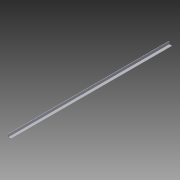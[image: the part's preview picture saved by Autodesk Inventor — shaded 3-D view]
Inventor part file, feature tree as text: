
AUTODESK INVENTOR PART (.ipt)
format: ipt  version: 2014 SP1 (Build 180222100, 222)  size: 81,920 bytes
history: native  units: in
note: dims shown in document units (in); Inventor stores cm internally (conversion verified against a paired STEP export)
features: extrude x1, sketch x1
ambient origin geometry x8: Origin, YZ Plane, XZ Plane, XY Plane, X Axis, Y Axis, Z Axis, Center Point
bodies: Solid1 (feature_tree)
feature tree (2):
  extrude  "Extrusion1"  Depth=0.0625in
  sketch  "Sketch1"  dims[d0=0.5in d1=0.0625in d2=0.5in d3=0.0625in d4=26.75in d5=0.0in]
